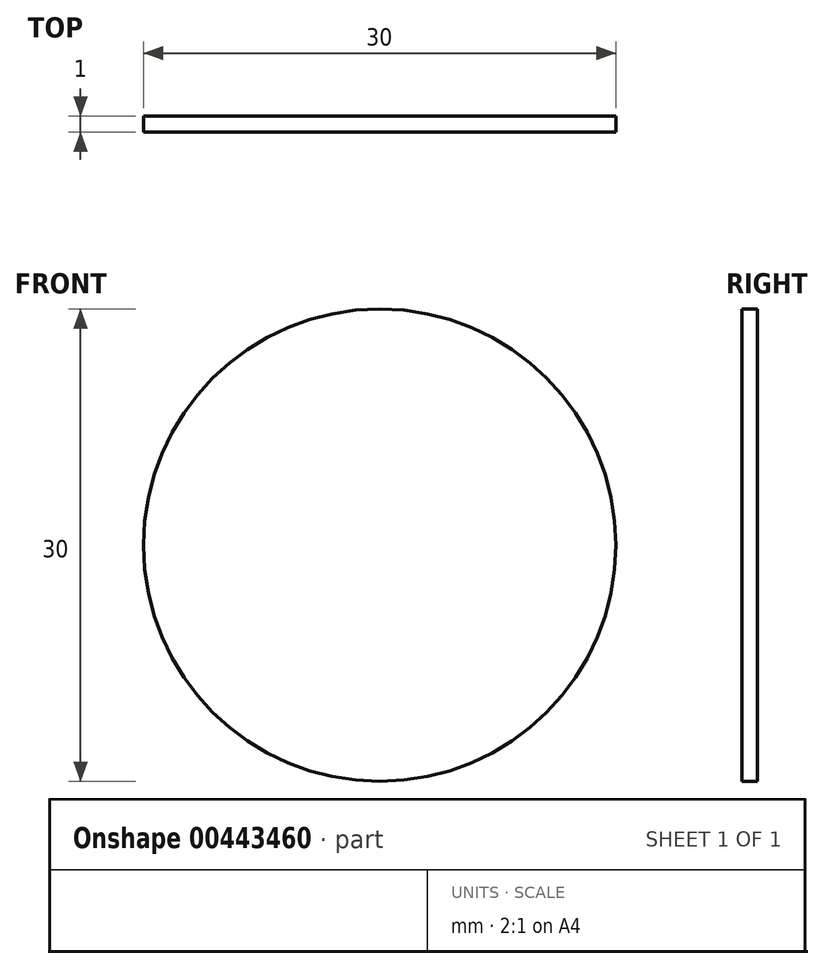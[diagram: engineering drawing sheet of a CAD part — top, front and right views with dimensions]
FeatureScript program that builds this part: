
annotation { "Feature Type Name" : "Feature", "Feature Type Description" : "" }
export const myFeature = defineFeature(function(context is Context, id is Id, definition is map)
    precondition{}
    {
        {
            var Q0;
            Q0=qCreatedBy(makeId("Front.planeOp"),FACE);
            var sketch = newSketch(context, id + "F0", { "sketchPlane" : qUnion([Q0])});
            skCircle(sketch, "E0", {"center": v(0, 0) * mm, "radius": 15 * mm});
            skSolve(sketch);
        }
        {
            var Q0;
            Q0 = qSketchRegion(id + "F0", true);
            extrude(context, id + "F1", {"entities" : qUnion([Q0]), "depth" : 1 * mm});
        }
    });
